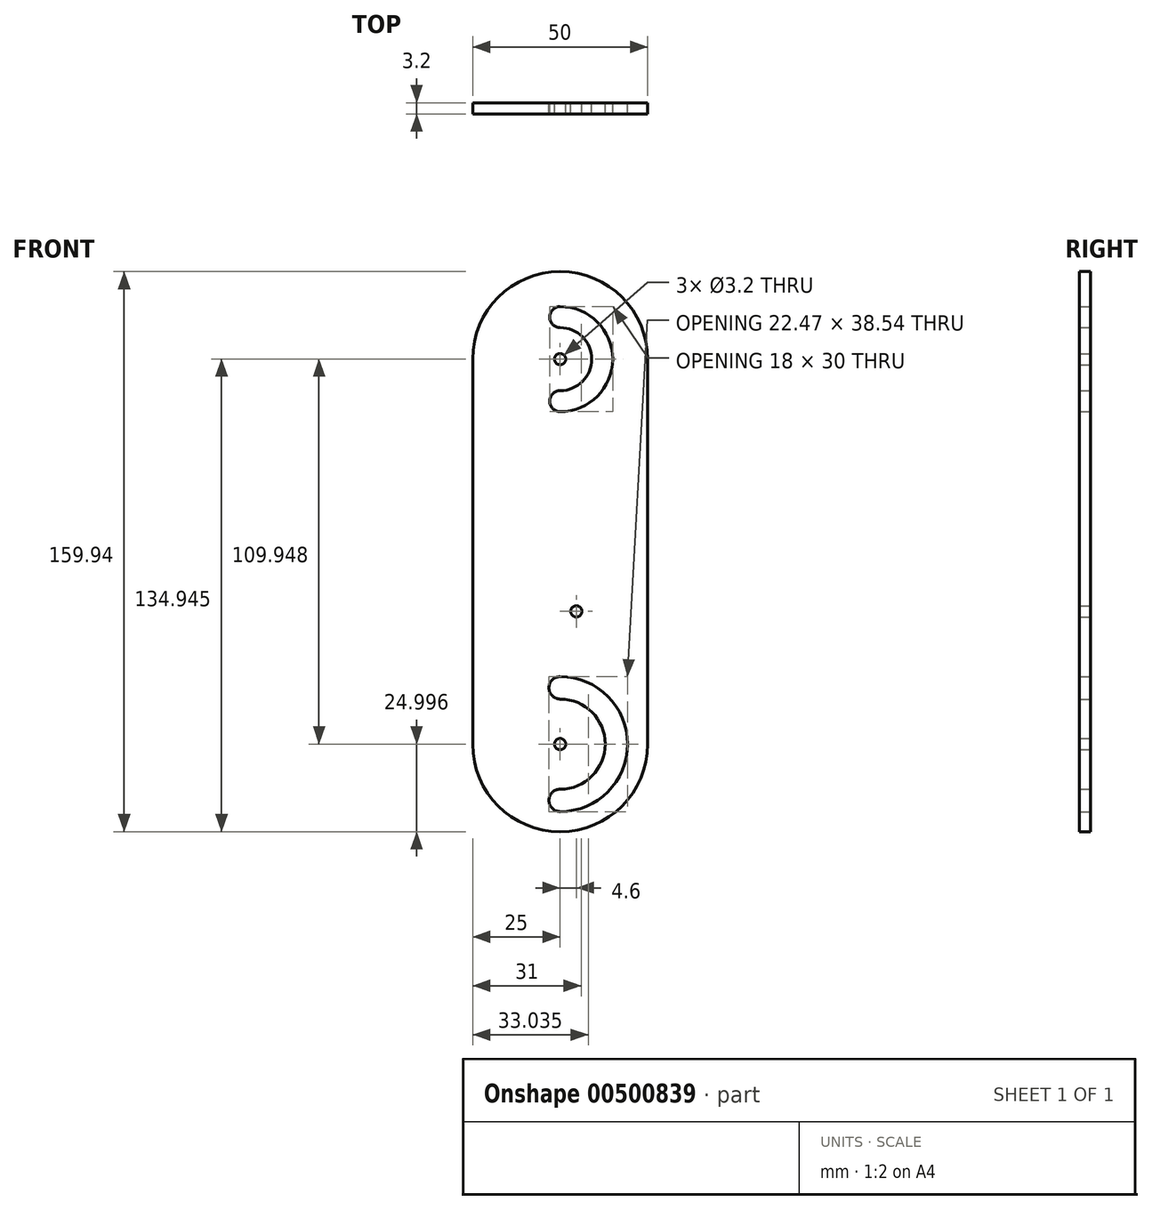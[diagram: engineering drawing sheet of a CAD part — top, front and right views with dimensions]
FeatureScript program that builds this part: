
annotation { "Feature Type Name" : "Feature", "Feature Type Description" : "" }
export const myFeature = defineFeature(function(context is Context, id is Id, definition is map)
    precondition{}
    {
        {
            var Q0;
            Q0=qCreatedBy(makeId("Front.planeOp"),FACE);
            var sketch = newSketch(context, id + "F0", { "sketchPlane" : qUnion([Q0])});
            skLineSegment(sketch, "E0", {"start": v(-25, 56.11) * mm, "end": v(-25, -53.83) * mm});
            skLineSegment(sketch, "E1", {"start": v(25, -53.83) * mm, "end": v(25, 56.11) * mm});
            skCircle(sketch, "E2", {"center": v(0, 56.11) * mm, "radius": 1.6 * mm});
            skCircle(sketch, "E3", {"center": v(0, -53.83) * mm, "radius": 1.6 * mm});
            skLineSegment(sketch, "E4", {"start": v(0, 0) * mm, "end": v(0, -53.83) * mm, "construction": true});
            skLineSegment(sketch, "E5", {"start": v(0, -53.83) * mm, "end": v(19.27, -53.83) * mm, "construction": true});
            skLineSegment(sketch, "E6", {"start": v(0, -53.83) * mm, "end": v(12.87, -53.83) * mm, "construction": true});
            skLineSegment(sketch, "E7", {"start": v(12.87, -53.83) * mm, "end": v(19.27, -53.83) * mm, "construction": true});
            skPoint(sketch, "E8", {"position": v(16.07, -53.83) * mm});
            skLineSegment(sketch, "E9", {"start": v(19.27, -53.83) * mm, "end": v(19.27, -66.7) * mm, "construction": true});
            skLineSegment(sketch, "E10", {"start": v(19.27, -66.7) * mm, "end": v(0, -66.7) * mm, "construction": true});
            skLineSegment(sketch, "E11", {"start": v(12.87, -53.83) * mm, "end": v(12.87, -73.1) * mm, "construction": true});
            skLineSegment(sketch, "E12", {"start": v(12.87, -73.1) * mm, "end": v(0, -73.1) * mm, "construction": true});
            skArc(sketch, "E13", {"start": v(0, -66.7) * mm, "mid": v(9.1, -62.93) * mm, "end": v(12.87, -53.83) * mm});
            skArc(sketch, "E14", {"start": v(0, -73.1) * mm, "mid": v(13.63, -67.46) * mm, "end": v(19.27, -53.83) * mm});
            skArc(sketch, "E15", {"start": v(0, -66.7) * mm, "mid": v(-3.2, -69.9) * mm, "end": v(0, -73.1) * mm});
            skArc(sketch, "E16.MirrorCS", {"start": v(0, -40.96) * mm, "mid": v(-3.2, -37.76) * mm, "end": v(0, -34.56) * mm});
            skArc(sketch, "E17.MirrorCS", {"start": v(0, -34.56) * mm, "mid": v(13.63, -40.2) * mm, "end": v(19.27, -53.83) * mm});
            skArc(sketch, "E18.MirrorCS", {"start": v(0, -40.96) * mm, "mid": v(9.1, -44.73) * mm, "end": v(12.87, -53.83) * mm});
            skArc(sketch, "E19", {"start": v(-25, -53.83) * mm, "mid": v(0, -78.83) * mm, "end": v(25, -53.83) * mm});
            skArc(sketch, "E20", {"start": v(25, 56.11) * mm, "mid": v(0, 81.11) * mm, "end": v(-25, 56.11) * mm});
            skLineSegment(sketch, "E21", {"start": v(0, 56.11) * mm, "end": v(12, 56.11) * mm, "construction": true});
            skCircle(sketch, "E22", {"center": v(12, 56.11) * mm, "radius": 3 * mm, "construction": true});
            skPoint(sketch, "E23", {"position": v(9, 56.11) * mm});
            skPoint(sketch, "E24", {"position": v(15, 56.11) * mm});
            skLineSegment(sketch, "E25", {"start": v(0, 56.11) * mm, "end": v(0, 68.11) * mm, "construction": true});
            skPoint(sketch, "E26", {"position": v(0, 65.11) * mm});
            skPoint(sketch, "E27", {"position": v(0, 71.11) * mm});
            skLineSegment(sketch, "E28", {"start": v(15, 56.11) * mm, "end": v(15, 71.11) * mm, "construction": true});
            skLineSegment(sketch, "E29", {"start": v(15, 71.11) * mm, "end": v(0, 71.11) * mm, "construction": true});
            skLineSegment(sketch, "E30", {"start": v(0, 65.11) * mm, "end": v(9, 65.11) * mm, "construction": true});
            skLineSegment(sketch, "E31", {"start": v(9, 65.11) * mm, "end": v(9, 56.11) * mm, "construction": true});
            skLineSegment(sketch, "E32.MirrorCS", {"start": v(0, 56.11) * mm, "end": v(0, 44.11) * mm, "construction": true});
            skLineSegment(sketch, "E33.MirrorCS", {"start": v(0, 47.11) * mm, "end": v(9, 47.11) * mm, "construction": true});
            skLineSegment(sketch, "E34.MirrorCS", {"start": v(15, 41.11) * mm, "end": v(0, 41.11) * mm, "construction": true});
            skLineSegment(sketch, "E35.MirrorCS", {"start": v(15, 56.11) * mm, "end": v(15, 41.11) * mm, "construction": true});
            skLineSegment(sketch, "E36.MirrorCS", {"start": v(9, 47.11) * mm, "end": v(9, 56.11) * mm, "construction": true});
            skArc(sketch, "E37", {"start": v(0, 47.11) * mm, "mid": v(9, 56.11) * mm, "end": v(0, 65.11) * mm});
            skArc(sketch, "E38", {"start": v(0, 41.11) * mm, "mid": v(15, 56.11) * mm, "end": v(0, 71.11) * mm});
            skArc(sketch, "E39", {"start": v(0, 71.11) * mm, "mid": v(-3, 68.11) * mm, "end": v(0, 65.11) * mm});
            skArc(sketch, "E40", {"start": v(0, 47.11) * mm, "mid": v(-3, 44.11) * mm, "end": v(0, 41.11) * mm});
            skLineSegment(sketch, "E41", {"start": v(0, 44.11) * mm, "end": v(0, 0) * mm, "construction": true});
            skCircle(sketch, "E42", {"center": v(4.6, -15.92) * mm, "radius": 1.6 * mm});
            skSolve(sketch);
        }
        {
            var Q0;
            Q0 = qSketchRegion(id + "F0", true);
            extrude(context, id + "F1", {"entities" : qUnion([Q0]), "depth" : 3.2 * mm, "offsetDistance" : 25 * mm});
        }
    });
